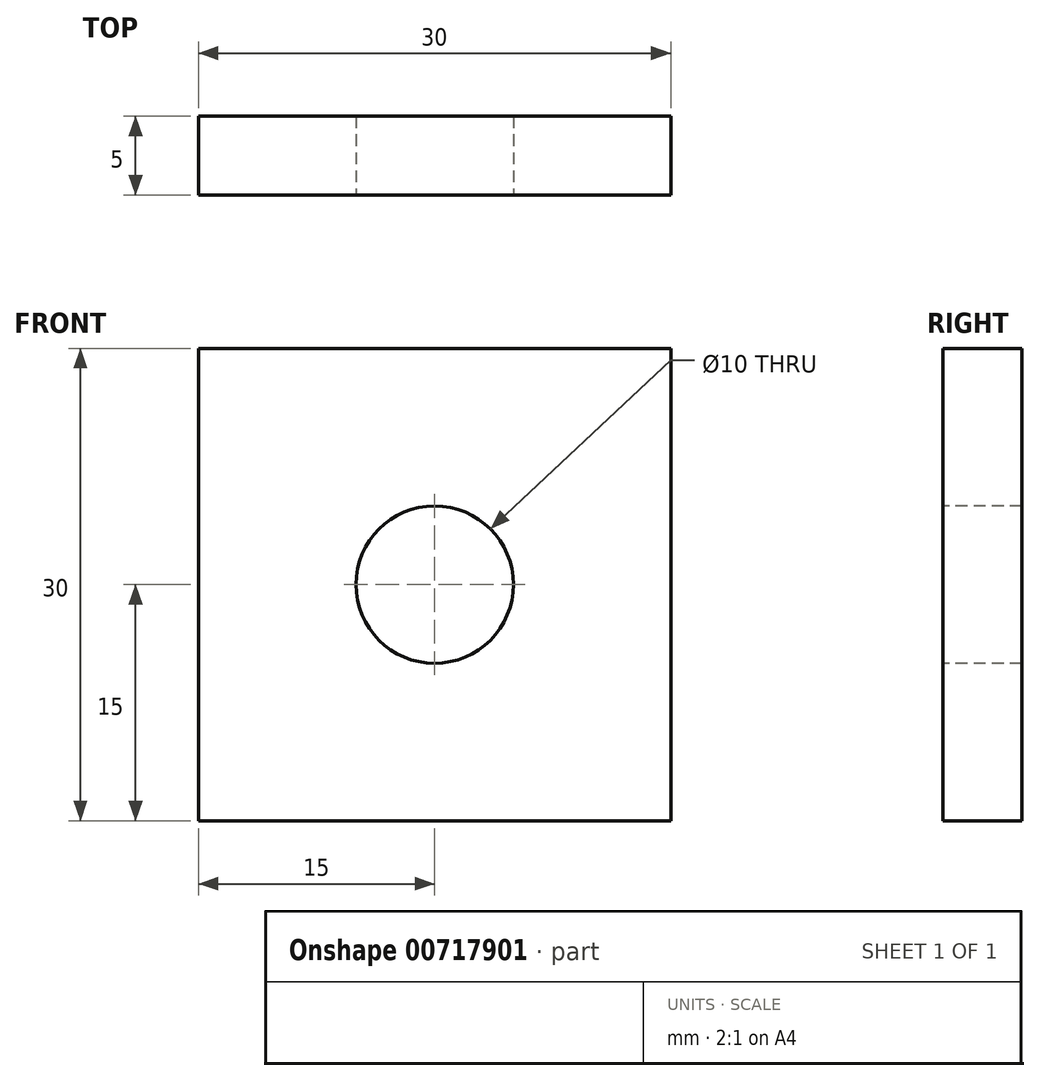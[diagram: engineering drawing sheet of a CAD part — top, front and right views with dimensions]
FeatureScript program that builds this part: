
annotation { "Feature Type Name" : "Feature", "Feature Type Description" : "" }
export const myFeature = defineFeature(function(context is Context, id is Id, definition is map)
    precondition{}
    {
        {
            var Q0;
            Q0=qCreatedBy(makeId("Front.planeOp"),FACE);
            var sketch = newSketch(context, id + "F0", { "sketchPlane" : qUnion([Q0])});
            skLineSegment(sketch, "E0.bottom", {"start": v(15, -15) * mm, "end": v(-15, -15) * mm});
            skLineSegment(sketch, "E0.top", {"start": v(15, 15) * mm, "end": v(-15, 15) * mm});
            skLineSegment(sketch, "E0.left", {"start": v(15, -15) * mm, "end": v(15, 15) * mm});
            skLineSegment(sketch, "E0.right", {"start": v(-15, -15) * mm, "end": v(-15, 15) * mm});
            skPoint(sketch, "E0.middle", {"position": v(0, 0) * mm});
            skPoint(sketch, "E1", {"position": v(0, 10.94) * mm});
            skCircle(sketch, "E2", {"center": v(0, 0) * mm, "radius": 5 * mm});
            skSolve(sketch);
        }
        {
            var Q0;
            Q0 = qSketchRegion(id + "F0", true);
            extrude(context, id + "F1", {"entities" : qUnion([Q0]), "oppositeDirection" : true, "depth" : 5 * mm, "offsetDistance" : 25 * mm});
        }
    });
